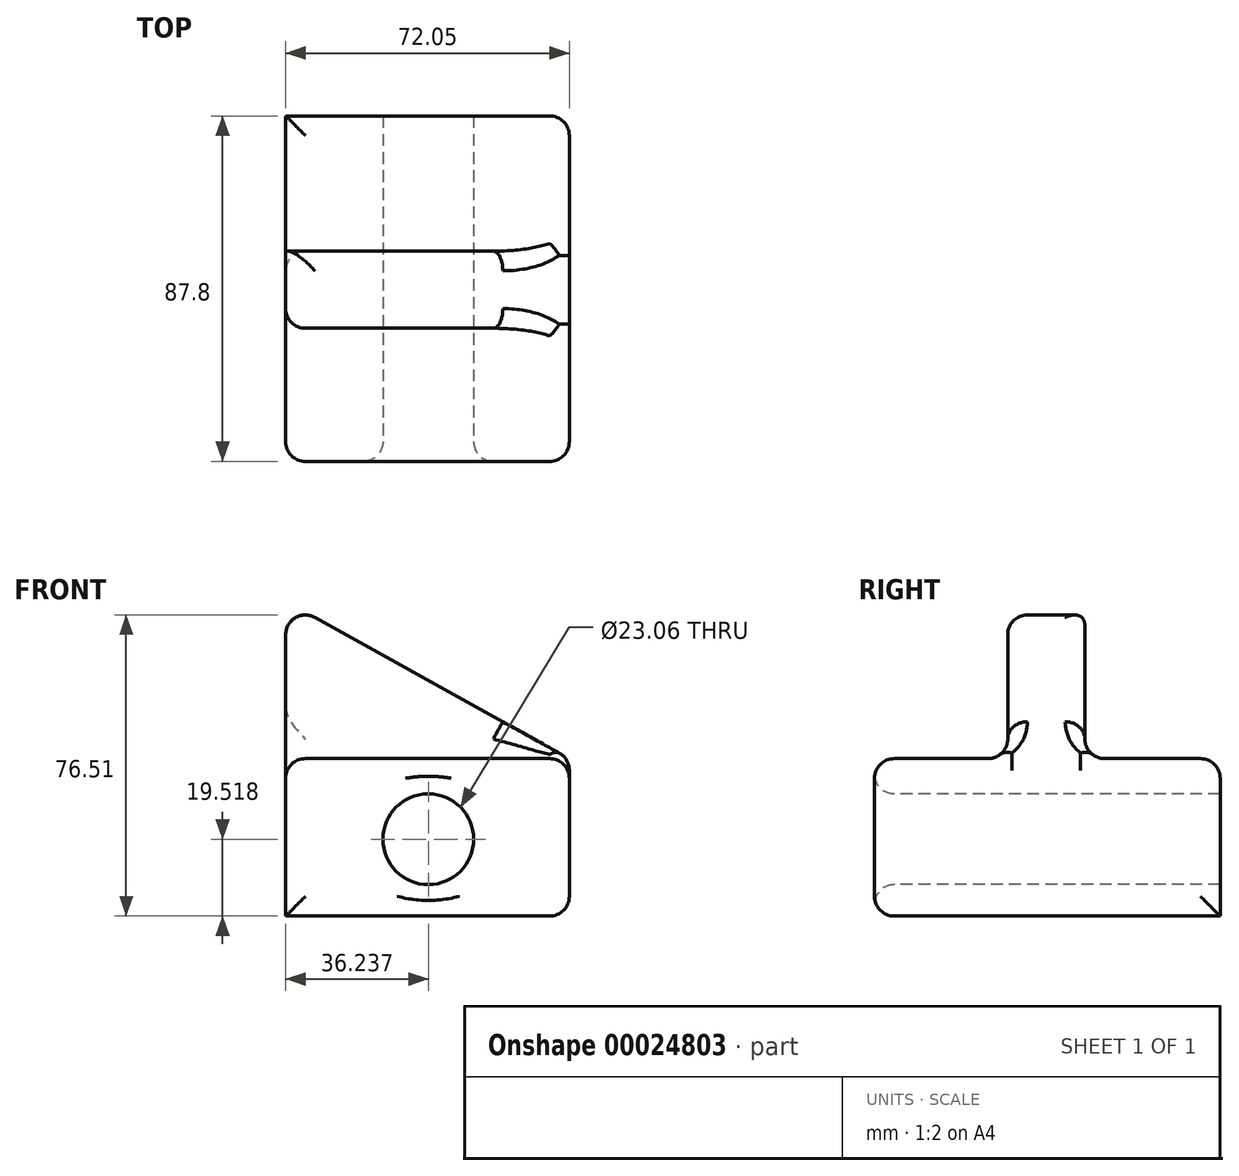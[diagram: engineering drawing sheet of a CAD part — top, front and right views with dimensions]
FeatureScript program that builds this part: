
annotation { "Feature Type Name" : "Feature", "Feature Type Description" : "" }
export const myFeature = defineFeature(function(context is Context, id is Id, definition is map)
    precondition{}
    {
        {
            var Q0;
            Q0=qCreatedBy(makeId("Top.planeOp"),FACE);
            var sketch = newSketch(context, id + "F0", { "sketchPlane" : qUnion([Q0])});
            skLineSegment(sketch, "E0.bottom", {"start": v(-59.89, -44.54) * mm, "end": v(12.16, -44.54) * mm});
            skLineSegment(sketch, "E0.top", {"start": v(-59.89, 43.26) * mm, "end": v(12.16, 43.26) * mm});
            skLineSegment(sketch, "E0.left", {"start": v(-59.89, -44.54) * mm, "end": v(-59.89, 43.26) * mm});
            skLineSegment(sketch, "E0.right", {"start": v(12.16, -44.54) * mm, "end": v(12.16, 43.26) * mm});
            skSolve(sketch);
        }
        {
            var Q0;
            Q0=makeQuery(id+"F0.imprint","IMPRINT",FACE,{"disambiguationData":[TD([[makeQuery(id+"F0.imprint","IMPRINT",EDGE,{"derivedFrom":sQuery(id+"F0.wireOp",EDGE,"E0.bottom")}),1.0]])]});
            extrude(context, id + "F1", {"entities" : qUnion([Q0]), "depth" : 40 * mm});
        }
        {
            var Q0;
            Q0=makeQuery(id+"F1.opExtrude","SWEPT_FACE",FACE,{"disambiguationData":[OSD([sQuery(id+"F0.wireOp",EDGE,"E0.bottom")])]});
            var sketch = newSketch(context, id + "F2", { "sketchPlane" : qUnion([Q0])});
            skCircle(sketch, "E1", {"center": v(-23.65, 19.52) * mm, "radius": 11.53 * mm});
            skSolve(sketch);
        }
        {
            var Q0;
            Q0=makeQuery(id+"F2.imprint","IMPRINT",FACE,{"disambiguationData":[TD([[makeQuery(id+"F2.imprint","IMPRINT",EDGE,{"derivedFrom":sQuery(id+"F2.wireOp",EDGE,"E1")}),1.0]])]});
            extrude(context, id + "F3", {"entities" : qUnion([Q0]), "operationType" : NewBodyOperationType.REMOVE, "endBound" : BoundingType.THROUGH_ALL, "oppositeDirection" : true, "depth" : 25 * mm});
        }
        {
            var Q0;
            Q0=makeQuery(id+"F1.opExtrude","CAP_FACE",FACE,{"disambiguationData":[OSD([sQuery(id+"F0.wireOp",EDGE,"E0.bottom"),sQuery(id+"F0.wireOp",EDGE,"E0.top"),sQuery(id+"F0.wireOp",EDGE,"E0.left"),sQuery(id+"F0.wireOp",EDGE,"E0.right")])],"isStart":false});
            var sketch = newSketch(context, id + "F4", { "sketchPlane" : qUnion([Q0])});
            skLineSegment(sketch, "E2.bottom", {"start": v(-59.89, -10.7) * mm, "end": v(12.16, -10.7) * mm});
            skLineSegment(sketch, "E2.top", {"start": v(-59.89, 8.88) * mm, "end": v(12.16, 8.88) * mm});
            skLineSegment(sketch, "E2.left", {"start": v(-59.89, -10.7) * mm, "end": v(-59.89, 8.88) * mm});
            skLineSegment(sketch, "E2.right", {"start": v(12.16, -10.7) * mm, "end": v(12.16, 8.88) * mm});
            skSolve(sketch);
        }
        {
            var Q0;
            Q0=makeQuery(id+"F4.imprint","IMPRINT",FACE,{"disambiguationData":[TD([[makeQuery(id+"F4.imprint","IMPRINT",EDGE,{"derivedFrom":sQuery(id+"F4.wireOp",EDGE,"E2.bottom")}),1.0]])]});
            extrude(context, id + "F5", {"entities" : qUnion([Q0]), "operationType" : NewBodyOperationType.ADD, "depth" : 40 * mm});
        }
        {
            var Q0;
            Q0=makeQuery(id+"F5.opExtrude","SWEPT_FACE",FACE,{"disambiguationData":[OSD([sQuery(id+"F4.wireOp",EDGE,"E2.bottom")])]});
            var sketch = newSketch(context, id + "F6", { "sketchPlane" : qUnion([Q0])});
            skLineSegment(sketch, "E3", {"start": v(12.16, 40) * mm, "end": v(-59.89, 80) * mm});
            skSolve(sketch);
        }
        {
            var Q0;
            Q0=makeQuery(id+"F6.imprint","IMPRINT",FACE,{"disambiguationData":[TD([[makeQuery(id+"F6.imprint","IMPRINT",EDGE,{"derivedFrom":sQuery(id+"F6.wireOp",EDGE,"E3")}),-1.0]])]});
            extrude(context, id + "F7", {"entities" : qUnion([Q0]), "operationType" : NewBodyOperationType.REMOVE, "endBound" : BoundingType.THROUGH_ALL, "oppositeDirection" : true, "depth" : 25 * mm});
        }
        {
            var Q0;
            Q0=makeQuery(id+"F5.opExtrude","SWEPT_FACE",FACE,{"disambiguationData":[OSD([sQuery(id+"F4.wireOp",EDGE,"E2.bottom")])]});
            var Q1;
            Q1=makeQuery(id+"F7.boolean.opBoolean","COPY",FACE,{"derivedFrom":makeQuery(id+"F7.opExtrude","SWEPT_FACE",FACE,{"disambiguationData":[OSD([sQuery(id+"F6.wireOp",EDGE,"E3")])]})});
            var Q2;
            {var subQ0=sQuery(id+"F0.wireOp",EDGE,"E0.top");var subQ1=sQuery(id+"F0.wireOp",EDGE,"E0.left");var subQ2=sQuery(id+"F0.wireOp",EDGE,"E0.right");Q2=makeQuery(id+"F5.boolean.opBoolean","SPLIT",FACE,{"disambiguationData":[TD([makeQuery(id+"F1.opExtrude","SWEPT_FACE",FACE,{"disambiguationData":[OSD([subQ0])]})])],"derivedFrom":makeQuery(id+"F1.opExtrude","CAP_FACE",FACE,{"disambiguationData":[OSD([sQuery(id+"F0.wireOp",EDGE,"E0.bottom"),subQ0,subQ1,subQ2])],"isStart":false})});}
            var Q3;
            {var subQ0=sQuery(id+"F0.wireOp",EDGE,"E0.bottom");var subQ1=sQuery(id+"F0.wireOp",EDGE,"E0.left");var subQ2=sQuery(id+"F0.wireOp",EDGE,"E0.right");Q3=makeQuery(id+"F5.boolean.opBoolean","SPLIT",FACE,{"disambiguationData":[TD([makeQuery(id+"F1.opExtrude","SWEPT_FACE",FACE,{"disambiguationData":[OSD([subQ0])]})])],"derivedFrom":makeQuery(id+"F1.opExtrude","CAP_FACE",FACE,{"disambiguationData":[OSD([subQ0,sQuery(id+"F0.wireOp",EDGE,"E0.top"),subQ1,subQ2])],"isStart":false})});}
            var Q4;
            Q4=makeQuery(id+"F5.boolean.opBoolean","MERGE",FACE,{"derivedFrom":[makeQuery(id+"F1.opExtrude","SWEPT_FACE",FACE,{"disambiguationData":[OSD([sQuery(id+"F0.wireOp",EDGE,"E0.right")])]}),makeQuery(id+"F5.opExtrude","SWEPT_FACE",FACE,{"disambiguationData":[OSD([sQuery(id+"F4.wireOp",EDGE,"E2.right")])]})]});
            var Q5;
            Q5=makeQuery(id+"F1.opExtrude","SWEPT_FACE",FACE,{"disambiguationData":[OSD([sQuery(id+"F0.wireOp",EDGE,"E0.bottom")])]});
            fillet(context, id + "F8", {"entities" : qUnion([Q0, Q1, Q2, Q3, Q4, Q5]), "radius" : 5 * mm, "tangentPropagation" : true, "allowEdgeOverflow" : false});
        }
    });
